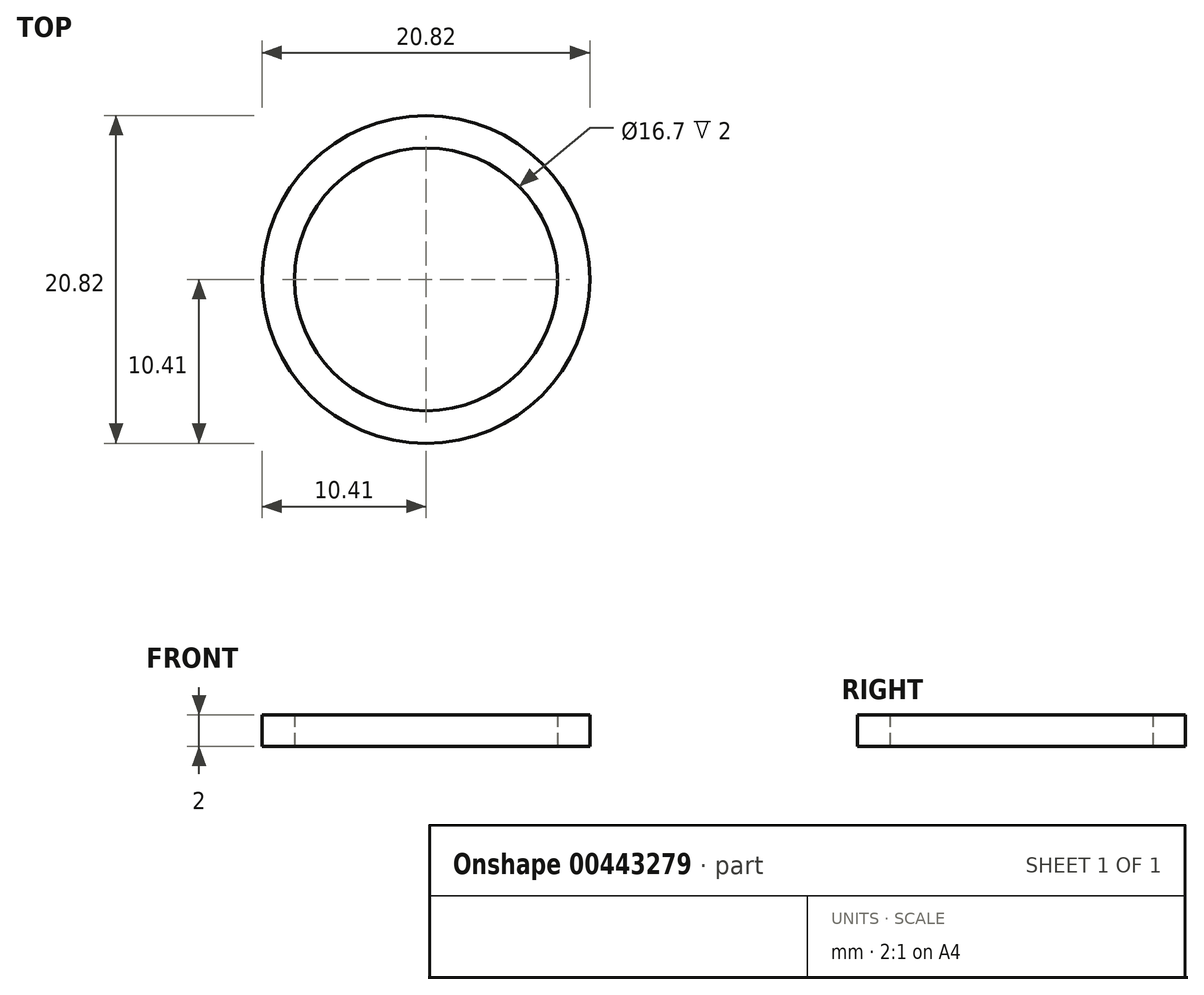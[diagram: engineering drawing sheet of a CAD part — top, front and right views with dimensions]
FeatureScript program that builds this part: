
annotation { "Feature Type Name" : "Feature", "Feature Type Description" : "" }
export const myFeature = defineFeature(function(context is Context, id is Id, definition is map)
    precondition{}
    {
        {
            var Q0;
            Q0=qCreatedBy(makeId("Top.planeOp"),FACE);
            var sketch = newSketch(context, id + "F0", { "sketchPlane" : qUnion([Q0])});
            skCircle(sketch, "E0", {"center": v(0, 0) * mm, "radius": 8.35 * mm});
            skCircle(sketch, "E1.0", {"center": v(0, 0) * mm, "radius": 10.4 * mm});
            skSolve(sketch);
        }
        {
            var Q0;
            Q0=makeQuery(id+"F0.imprint","IMPRINT",FACE,{"disambiguationData":[TD([[makeQuery(id+"F0.imprint","IMPRINT",EDGE,{"derivedFrom":sQuery(id+"F0.wireOp",EDGE,"E0")}),-1.0]])]});
            extrude(context, id + "F1", {"entities" : qUnion([Q0]), "depth" : 2 * mm});
        }
    });
